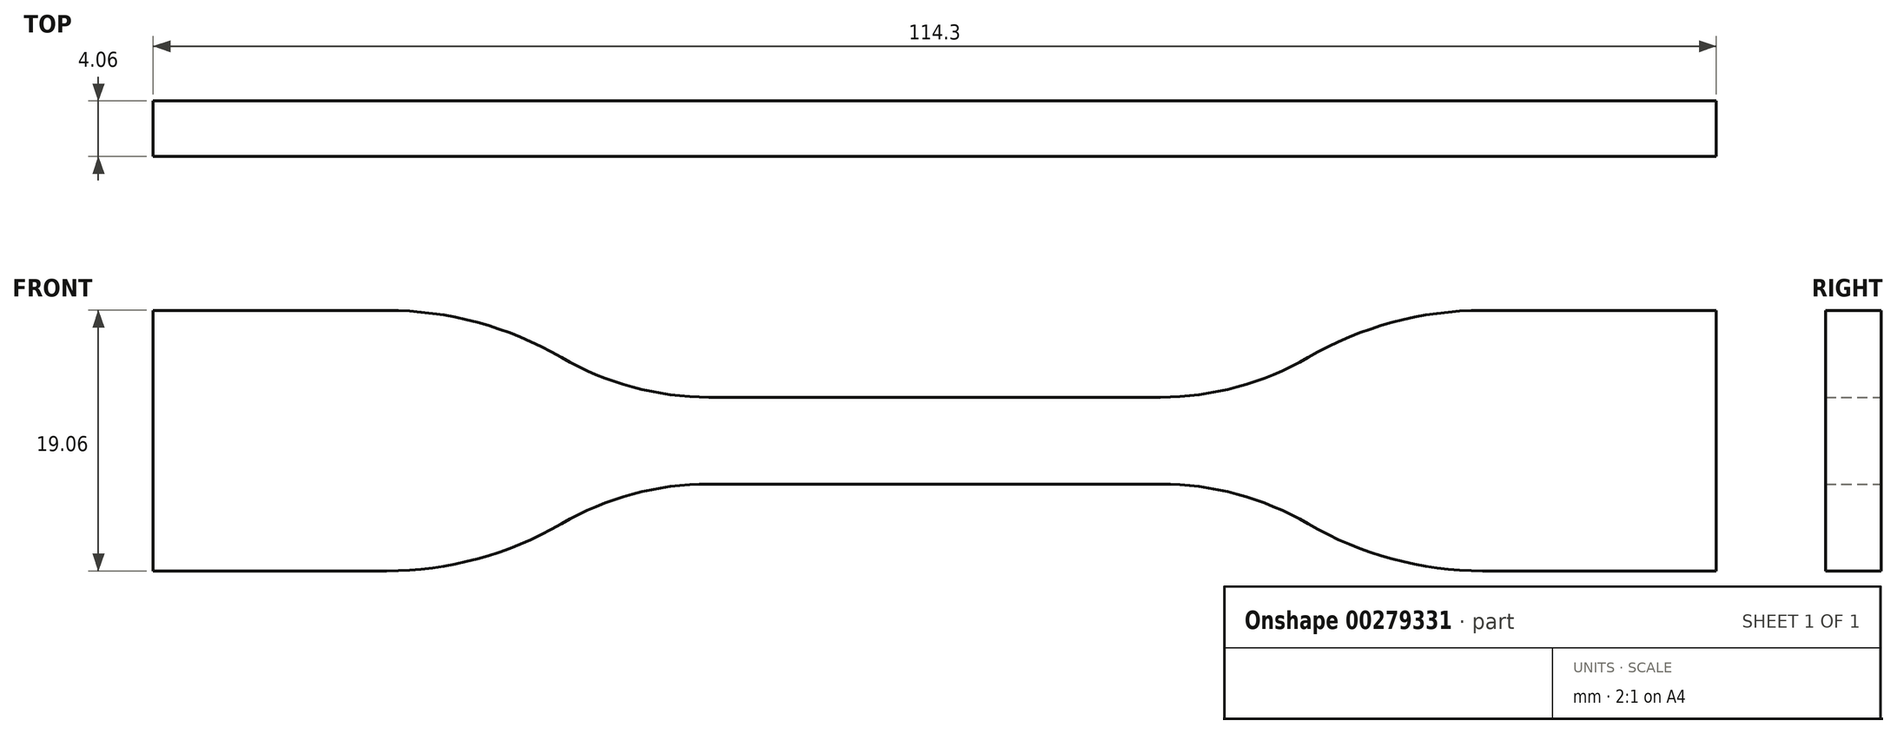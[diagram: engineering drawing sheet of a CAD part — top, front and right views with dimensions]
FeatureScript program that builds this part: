
annotation { "Feature Type Name" : "Feature", "Feature Type Description" : "" }
export const myFeature = defineFeature(function(context is Context, id is Id, definition is map)
    precondition{}
    {
        {
            var Q0;
            Q0=qCreatedBy(makeId("Front.planeOp"),FACE);
            var sketch = newSketch(context, id + "F0", { "sketchPlane" : qUnion([Q0])});
            skLineSegment(sketch, "E0", {"start": v(0, 3.18) * mm, "end": v(16.51, 3.18) * mm});
            skArc(sketch, "E1", {"start": v(16.51, 3.17) * mm, "mid": v(22.1, 3.91) * mm, "end": v(27.3, 6.08) * mm});
            skLineSegment(sketch, "E2", {"start": v(40.06, 9.53) * mm, "end": v(57.15, 9.53) * mm});
            skLineSegment(sketch, "E3.MirrorCS", {"start": v(40.06, -9.53) * mm, "end": v(57.15, -9.53) * mm});
            skLineSegment(sketch, "E4.MirrorCS", {"start": v(0, -3.18) * mm, "end": v(16.51, -3.18) * mm});
            skArc(sketch, "E5.MirrorCS", {"start": v(16.51, -3.17) * mm, "mid": v(22.1, -3.91) * mm, "end": v(27.3, -6.08) * mm});
            skArc(sketch, "E6.MirrorCS", {"start": v(-16.51, -3.17) * mm, "mid": v(-22.1, -3.91) * mm, "end": v(-27.3, -6.08) * mm});
            skLineSegment(sketch, "E7.MirrorCS", {"start": v(0, 3.18) * mm, "end": v(-16.51, 3.18) * mm});
            skArc(sketch, "E8.MirrorCS", {"start": v(-16.51, 3.18) * mm, "mid": v(-22.1, 3.91) * mm, "end": v(-27.3, 6.08) * mm});
            skLineSegment(sketch, "E9.MirrorCS", {"start": v(-40.06, -9.53) * mm, "end": v(-57.15, -9.53) * mm});
            skLineSegment(sketch, "E10.MirrorCS", {"start": v(0, -3.17) * mm, "end": v(-16.51, -3.17) * mm});
            skLineSegment(sketch, "E11.MirrorCS", {"start": v(-40.06, 9.53) * mm, "end": v(-57.15, 9.53) * mm});
            skLineSegment(sketch, "E12", {"start": v(-57.15, 9.53) * mm, "end": v(-57.15, -9.53) * mm});
            skLineSegment(sketch, "E13", {"start": v(57.15, 9.53) * mm, "end": v(57.15, -9.53) * mm});
            skPoint(sketch, "E14.visualSharp", {"position": v(-31.75, 9.53) * mm});
            skArc(sketch, "E14.filletArc", {"start": v(-27.3, 6.08) * mm, "mid": v(-33.45, 8.65) * mm, "end": v(-40.06, 9.52) * mm});
            skPoint(sketch, "E15.visualSharp", {"position": v(-31.75, -9.52) * mm});
            skArc(sketch, "E15.filletArc", {"start": v(-40.06, -9.53) * mm, "mid": v(-33.45, -8.65) * mm, "end": v(-27.3, -6.08) * mm});
            skPoint(sketch, "E16.visualSharp", {"position": v(31.75, 9.52) * mm});
            skArc(sketch, "E16.filletArc", {"start": v(40.06, 9.52) * mm, "mid": v(33.45, 8.65) * mm, "end": v(27.3, 6.08) * mm});
            skPoint(sketch, "E17.visualSharp", {"position": v(31.75, -9.53) * mm});
            skArc(sketch, "E17.filletArc", {"start": v(27.3, -6.08) * mm, "mid": v(33.45, -8.65) * mm, "end": v(40.06, -9.53) * mm});
            skSolve(sketch);
        }
        {
            var Q0;
            Q0=makeQuery(id+"F0.imprint","IMPRINT",FACE,{"disambiguationData":[TD([[makeQuery(id+"F0.imprint","IMPRINT",EDGE,{"derivedFrom":sQuery(id+"F0.wireOp",EDGE,"E0")}),-1.0]])]});
            extrude(context, id + "F1", {"entities" : qUnion([Q0]), "depth" : 4.06 * mm});
        }
    });
